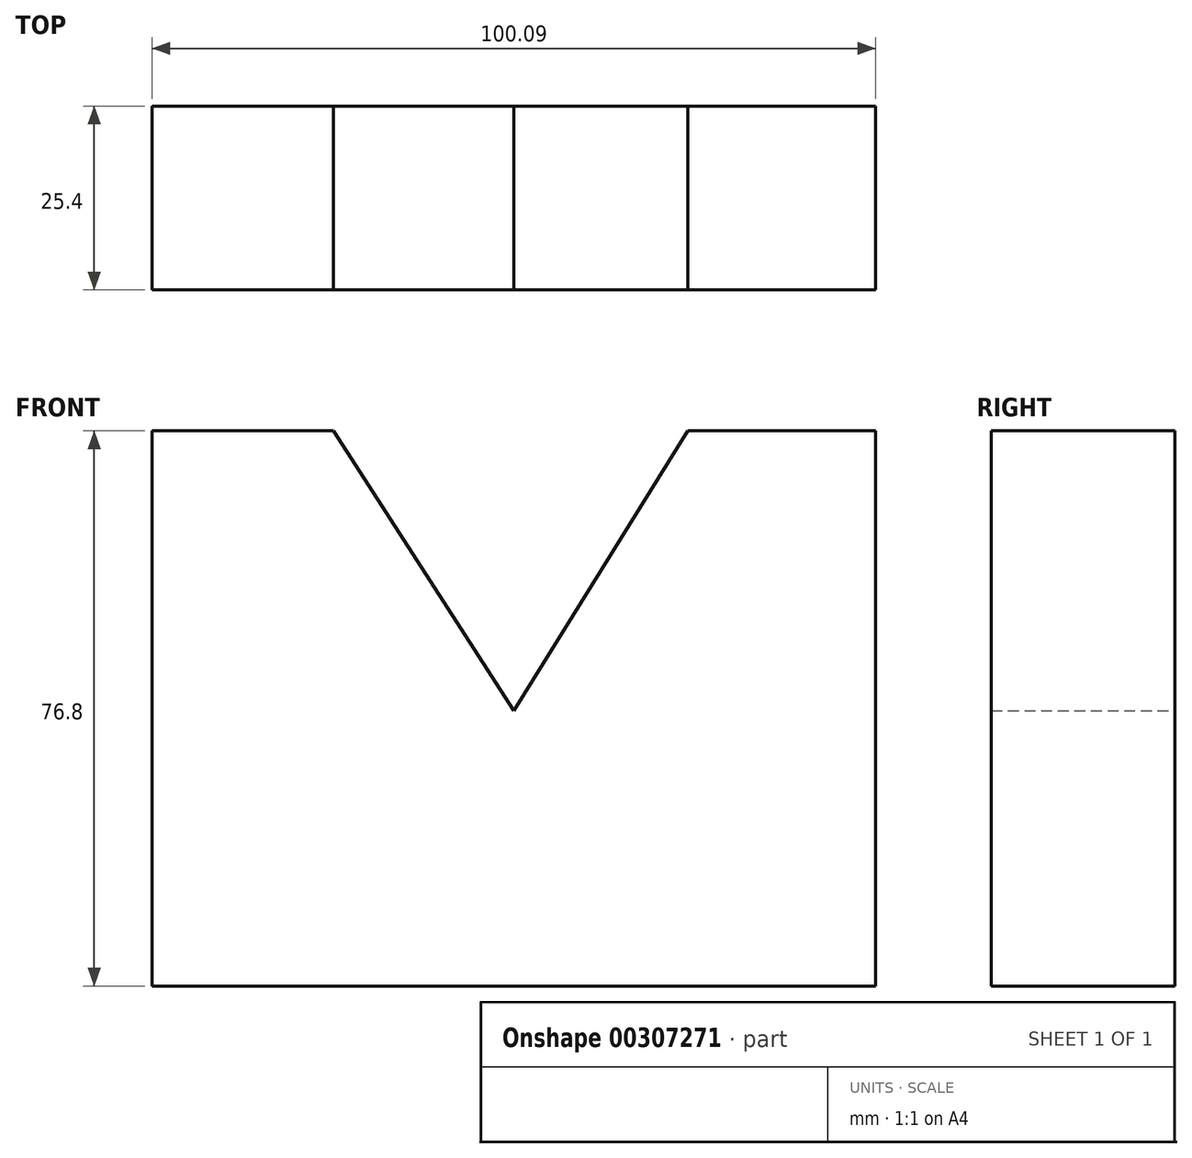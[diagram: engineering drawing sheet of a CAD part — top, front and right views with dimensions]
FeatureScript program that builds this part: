
annotation { "Feature Type Name" : "Feature", "Feature Type Description" : "" }
export const myFeature = defineFeature(function(context is Context, id is Id, definition is map)
    precondition{}
    {
        {
            var Q0;
            Q0=qCreatedBy(makeId("Front.planeOp"),FACE);
            var sketch = newSketch(context, id + "F0", { "sketchPlane" : qUnion([Q0])});
            skLineSegment(sketch, "E0", {"start": v(-38.75, -54.34) * mm, "end": v(61.34, -54.34) * mm});
            skLineSegment(sketch, "E1", {"start": v(61.34, -54.34) * mm, "end": v(61.34, 22.46) * mm});
            skLineSegment(sketch, "E2", {"start": v(61.34, 22.46) * mm, "end": v(35.34, 22.46) * mm});
            skLineSegment(sketch, "E3", {"start": v(-38.75, -54.34) * mm, "end": v(-38.75, 22.46) * mm});
            skLineSegment(sketch, "E4", {"start": v(-38.75, 22.46) * mm, "end": v(-13.65, 22.46) * mm});
            skLineSegment(sketch, "E5", {"start": v(35.34, 22.46) * mm, "end": v(11.3, -16.24) * mm});
            skLineSegment(sketch, "E6", {"start": v(-13.65, 22.46) * mm, "end": v(11.3, -16.24) * mm});
            skSolve(sketch);
        }
        {
            var Q0;
            Q0=makeQuery(id+"F0.imprint","IMPRINT",FACE,{"disambiguationData":[TD([[makeQuery(id+"F0.imprint","IMPRINT",EDGE,{"derivedFrom":sQuery(id+"F0.wireOp",EDGE,"E0")}),1.0]])]});
            extrude(context, id + "F1", {"entities" : qUnion([Q0]), "depth" : 25.4 * mm});
        }
    });
